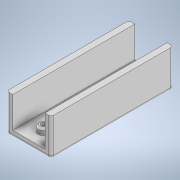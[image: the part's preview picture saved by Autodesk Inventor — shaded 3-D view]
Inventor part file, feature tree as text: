
AUTODESK INVENTOR PART (.ipt)
format: ipt  version: 2020 (Build 240168000, 168)  size: 185,856 bytes
history: native  units: in
note: dims shown in document units (in); Inventor stores cm internally (conversion verified against a paired STEP export)
features: extrude x5, sketch x5, chamfer x1, fillet x1
ambient origin geometry x8: Origin, YZ Plane, XZ Plane, XY Plane, X Axis, Y Axis, Z Axis, Center Point
bodies: Solid1 (feature_tree)
feature tree (12):
  extrude  "Extrusion1"  Depth=3.937in
  extrude  "Extrusion2"  Depth=0.1969in
  chamfer  "Chamfer1"  Distance=0.1969in
  extrude  "Extrusion3"  Depth=0.0787in TaperAngle=45.0deg
  extrude  "Extrusion4"  Depth=0.1969in
  extrude  "Extrusion5"  Depth=0.1969in
  fillet  "Fillet1"  Radius=1.0in
  sketch  "Sketch1"  dims[d0=1.4331in d1=3.937in]
  sketch  "Sketch2"  dims[d2=0.1969in d3=0.0in d4=0.3406in]
  sketch  "Sketch3"  dims[d5=0.3406in]
  sketch  "Sketch4"  dims[d6=0.3406in]
  sketch  "Sketch5"  dims[d7=0.3406in d8=0.1969in d9=0.0in d10=0.0591in d11=0.0787in d12=45.0deg d13=0.1969in d14=0.1969in d15=1.0in d16=0.0in d17=0.1575in d18=0.1575in d19=0.1575in d20=0.1575in d21=1.0in d22=0.0in d23=0.2362in d24=0.2362in d25=0.2362in d26=0.2362in d27=0.0984in d28=0.0in d29=0.0787in]
